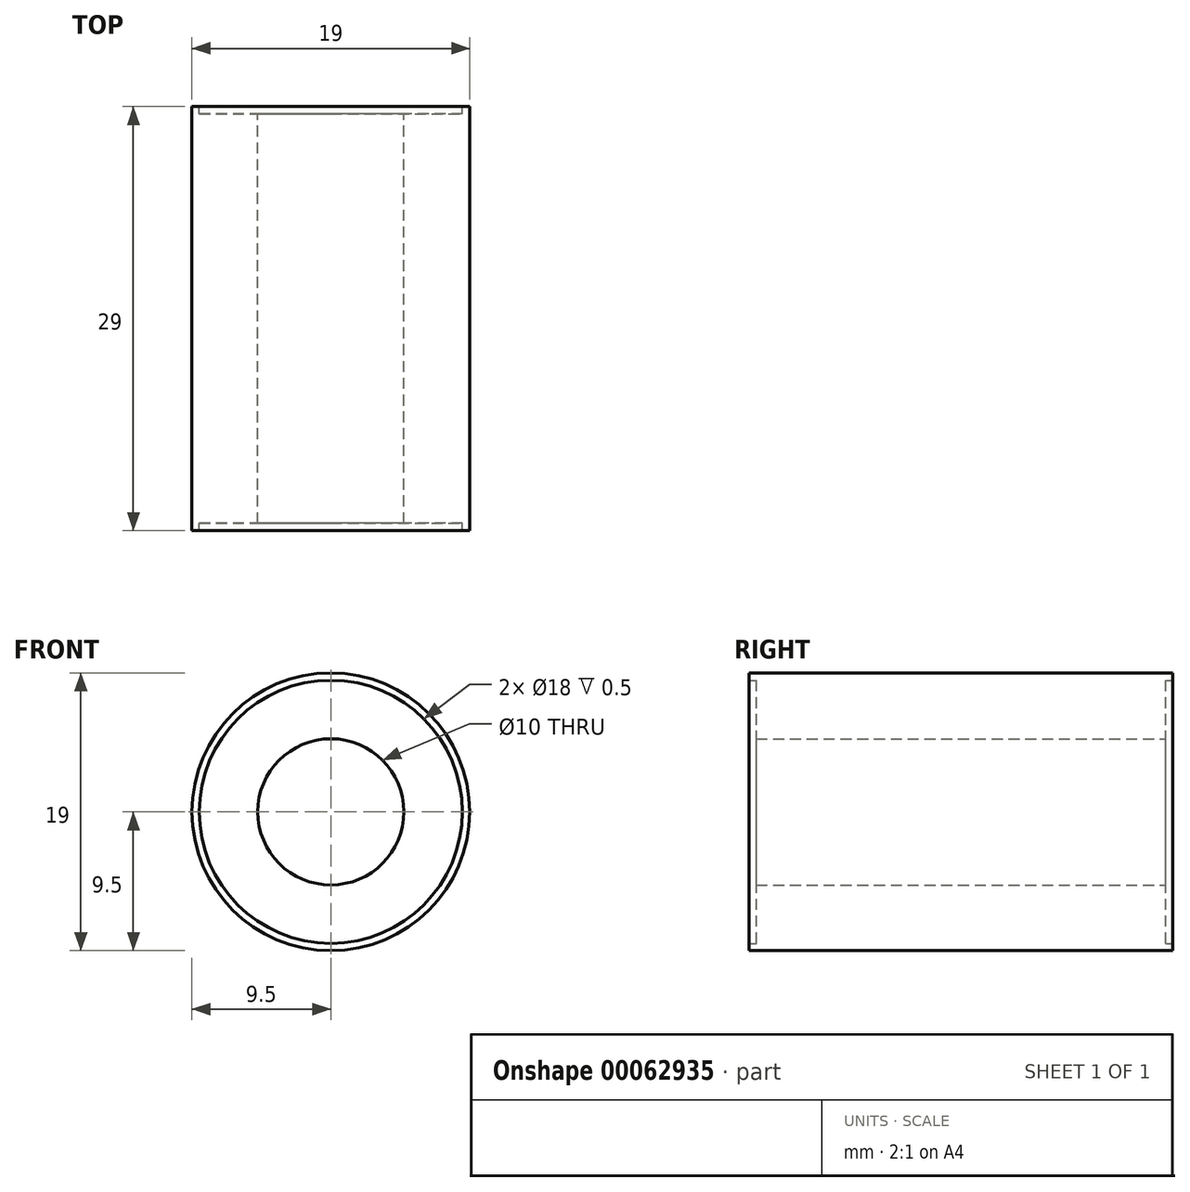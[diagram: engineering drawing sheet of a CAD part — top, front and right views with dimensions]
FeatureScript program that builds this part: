
annotation { "Feature Type Name" : "Feature", "Feature Type Description" : "" }
export const myFeature = defineFeature(function(context is Context, id is Id, definition is map)
    precondition{}
    {
        {
            var Q0;
            Q0=qCreatedBy(makeId("Front.planeOp"),FACE);
            var sketch = newSketch(context, id + "F0", { "sketchPlane" : qUnion([Q0])});
            skCircle(sketch, "E0", {"center": v(0, 0) * mm, "radius": 9 * mm});
            skCircle(sketch, "E1", {"center": v(0, 0) * mm, "radius": 9.5 * mm});
            skCircle(sketch, "E2", {"center": v(0, 0) * mm, "radius": 5 * mm});
            skSolve(sketch);
        }
        {
            var Q0;
            Q0=makeQuery(id+"F0.imprint","IMPRINT",FACE,{"disambiguationData":[TD([[makeQuery(id+"F0.imprint","IMPRINT",EDGE,{"derivedFrom":sQuery(id+"F0.wireOp",EDGE,"E0")}),1.0]])]});
            extrude(context, id + "F1", {"entities" : qUnion([Q0]), "depth" : 14 * mm, "hasSecondDirection" : true, "secondDirectionOppositeDirection" : true, "secondDirectionDepth" : 14 * mm});
        }
        {
            var Q0;
            Q0=makeQuery(id+"F0.imprint","IMPRINT",FACE,{"disambiguationData":[TD([[makeQuery(id+"F0.imprint","IMPRINT",EDGE,{"derivedFrom":sQuery(id+"F0.wireOp",EDGE,"E0")}),-1.0]])]});
            extrude(context, id + "F2", {"entities" : qUnion([Q0]), "operationType" : NewBodyOperationType.ADD, "depth" : 14.5 * mm, "hasSecondDirection" : true, "secondDirectionOppositeDirection" : true, "secondDirectionDepth" : 14.5 * mm});
        }
    });
